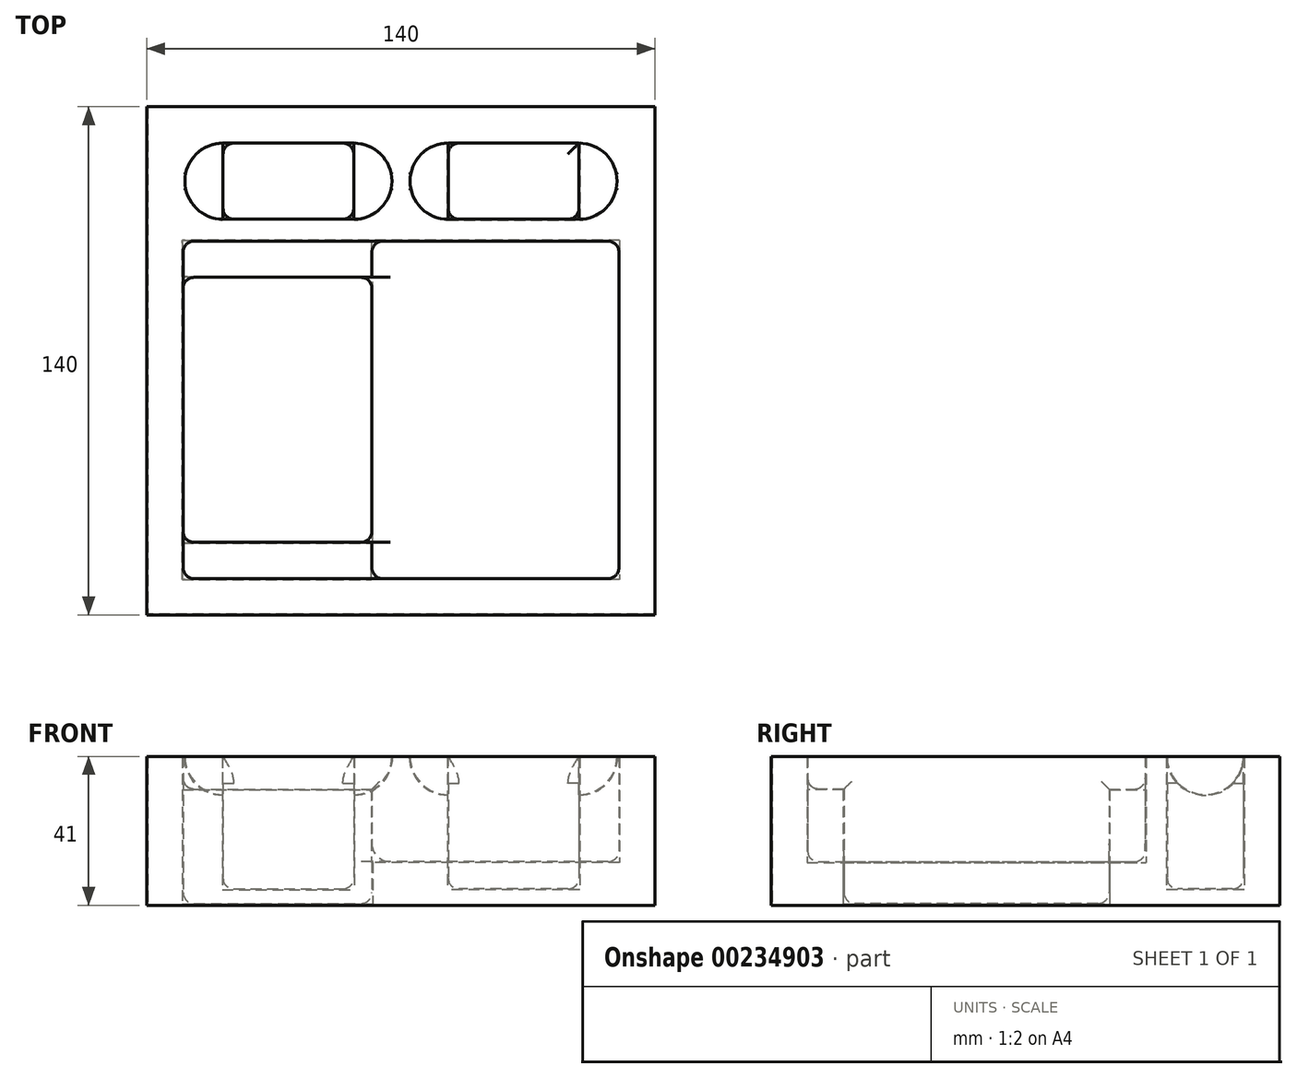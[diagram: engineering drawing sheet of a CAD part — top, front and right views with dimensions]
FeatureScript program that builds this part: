
annotation { "Feature Type Name" : "Feature", "Feature Type Description" : "" }
export const myFeature = defineFeature(function(context is Context, id is Id, definition is map)
    precondition{}
    {
        {
            var Q0;
            Q0=qCreatedBy(makeId("Top.planeOp"),FACE);
            cPlane(context, id + "F0", {"entities" : qUnion([Q0]), "cplaneType" : CPlaneType.OFFSET, "offset" : 4.5 * mm, "width" : 150 * mm, "height" : 150 * mm});
        }
        {
            var Q0;
            Q0=qCreatedBy(makeId("Top.planeOp"),FACE);
            cPlane(context, id + "F1", {"entities" : qUnion([Q0]), "cplaneType" : CPlaneType.OFFSET, "offset" : .5 * mm, "width" : 150 * mm, "height" : 150 * mm});
        }
        {
            var Q0;
            Q0=qCreatedBy(makeId("Top.planeOp"),FACE);
            cPlane(context, id + "F2", {"entities" : qUnion([Q0]), "cplaneType" : CPlaneType.OFFSET, "offset" : 12 * mm, "width" : 150 * mm, "height" : 150 * mm});
        }
        {
            var Q0;
            Q0=qCreatedBy(makeId("Top.planeOp"),FACE);
            cPlane(context, id + "F3", {"entities" : qUnion([Q0]), "cplaneType" : CPlaneType.OFFSET, "offset" : 32 * mm, "width" : 150 * mm, "height" : 150 * mm});
        }
        {
            var Q0;
            Q0=qCreatedBy(makeId("Top.planeOp"),FACE);
            var sketch = newSketch(context, id + "F4", { "sketchPlane" : qUnion([Q0])});
            skLineSegment(sketch, "E0.bottom", {"start": v(70, 70) * mm, "end": v(-70, 70) * mm});
            skLineSegment(sketch, "E0.top", {"start": v(70, -70) * mm, "end": v(-70, -70) * mm});
            skLineSegment(sketch, "E0.left", {"start": v(70, 70) * mm, "end": v(70, -70) * mm});
            skLineSegment(sketch, "E0.right", {"start": v(-70, 70) * mm, "end": v(-70, -70) * mm});
            skPoint(sketch, "E0.middle", {"position": v(0, 0) * mm});
            skLineSegment(sketch, "E1.0", {"start": v(60, 60) * mm, "end": v(60, -60) * mm, "construction": true});
            skLineSegment(sketch, "E1.1", {"start": v(60, 60) * mm, "end": v(-60, 60) * mm, "construction": true});
            skLineSegment(sketch, "E1.2", {"start": v(-60, 60) * mm, "end": v(-60, -60) * mm, "construction": true});
            skLineSegment(sketch, "E1.3", {"start": v(60, -60) * mm, "end": v(-60, -60) * mm, "construction": true});
            skSolve(sketch);
        }
        {
            var Q0;
            Q0 = qSketchRegion(id + "F4", true);
            extrude(context, id + "F5", {"entities" : qUnion([Q0]), "depth" : 41 * mm});
        }
        {
            var Q0;
            Q0=qCreatedBy(id+"F3.planeOp",FACE);
            var sketch = newSketch(context, id + "F6", { "sketchPlane" : qUnion([Q0])});
            skLineSegment(sketch, "E2.bottom", {"start": v(-60, -60) * mm, "end": v(33, -60) * mm});
            skLineSegment(sketch, "E2.top", {"start": v(-60, 33) * mm, "end": v(33, 33) * mm});
            skLineSegment(sketch, "E2.left", {"start": v(-60, -60) * mm, "end": v(-60, 33) * mm});
            skLineSegment(sketch, "E2.right", {"start": v(33, -60) * mm, "end": v(33, 33) * mm});
            skSolve(sketch);
        }
        {
            var Q0;
            Q0 = qSketchRegion(id + "F6", true);
            extrude(context, id + "F7", {"entities" : qUnion([Q0]), "operationType" : NewBodyOperationType.REMOVE, "endBound" : BoundingType.THROUGH_ALL, "depth" : 7.5 * mm});
        }
        {
            var Q0;
            Q0=qCreatedBy(id+"F0.planeOp",FACE);
            var sketch = newSketch(context, id + "F8", { "sketchPlane" : qUnion([Q0])});
            skLineSegment(sketch, "E3.bottom", {"start": v(-49, 60) * mm, "end": v(-13, 60) * mm});
            skLineSegment(sketch, "E3.top", {"start": v(-49, 39) * mm, "end": v(-13, 39) * mm});
            skLineSegment(sketch, "E3.left", {"start": v(-49, 60) * mm, "end": v(-49, 39) * mm});
            skLineSegment(sketch, "E3.right", {"start": v(-13, 60) * mm, "end": v(-13, 39) * mm});
            skLineSegment(sketch, "E4.MirrorCS", {"start": v(49, 39) * mm, "end": v(13, 39) * mm});
            skLineSegment(sketch, "E5.MirrorCS", {"start": v(49, 60) * mm, "end": v(13, 60) * mm});
            skLineSegment(sketch, "E6.MirrorCS", {"start": v(49, 60) * mm, "end": v(49, 39) * mm});
            skLineSegment(sketch, "E7.MirrorCS", {"start": v(13, 60) * mm, "end": v(13, 39) * mm});
            skSolve(sketch);
        }
        {
            var Q0;
            Q0 = qSketchRegion(id + "F8", true);
            extrude(context, id + "F9", {"entities" : qUnion([Q0]), "operationType" : NewBodyOperationType.REMOVE, "endBound" : BoundingType.THROUGH_ALL, "depth" : 35 * mm});
        }
        {
            var Q0;
            Q0=qCreatedBy(id+"F2.planeOp",FACE);
            var sketch = newSketch(context, id + "F10", { "sketchPlane" : qUnion([Q0])});
            skLineSegment(sketch, "E8.bottom", {"start": v(60, -60) * mm, "end": v(-8, -60) * mm});
            skLineSegment(sketch, "E8.top", {"start": v(60, 33) * mm, "end": v(-8, 33) * mm});
            skLineSegment(sketch, "E8.left", {"start": v(60, -60) * mm, "end": v(60, 33) * mm});
            skLineSegment(sketch, "E8.right", {"start": v(-8, -60) * mm, "end": v(-8, 33) * mm});
            skSolve(sketch);
        }
        {
            var Q0;
            Q0 = qSketchRegion(id + "F10", true);
            extrude(context, id + "F11", {"entities" : qUnion([Q0]), "operationType" : NewBodyOperationType.REMOVE, "endBound" : BoundingType.THROUGH_ALL, "depth" : 22 * mm});
        }
        {
            var Q0;
            Q0=qCreatedBy(id+"F1.planeOp",FACE);
            var sketch = newSketch(context, id + "F12", { "sketchPlane" : qUnion([Q0])});
            skLineSegment(sketch, "E9.bottom", {"start": v(-60, -50) * mm, "end": v(-8, -50) * mm});
            skLineSegment(sketch, "E9.top", {"start": v(-60, 23) * mm, "end": v(-8, 23) * mm});
            skLineSegment(sketch, "E9.left", {"start": v(-60, -50) * mm, "end": v(-60, 23) * mm});
            skLineSegment(sketch, "E10", {"start": v(-60, -13.5) * mm, "end": v(-65.69, -13.5) * mm, "construction": true});
            skPoint(sketch, "E10.endSnap0", {"position": v(-60, -13.5) * mm});
            skLineSegment(sketch, "E11", {"start": v(-8, 23) * mm, "end": v(-8, -50) * mm});
            skSolve(sketch);
        }
        {
            var Q0;
            Q0 = qSketchRegion(id + "F12", true);
            extrude(context, id + "F13", {"entities" : qUnion([Q0]), "operationType" : NewBodyOperationType.REMOVE, "endBound" : BoundingType.THROUGH_ALL, "depth" : 25 * mm});
        }
        {
            var Q0;
            Q0=makeQuery(id+"F5.opExtrude","CAP_FACE",FACE,{"disambiguationData":[OSD([sQuery(id+"F4.wireOp",EDGE,"E0.bottom"),sQuery(id+"F4.wireOp",EDGE,"E0.top"),sQuery(id+"F4.wireOp",EDGE,"E0.left"),sQuery(id+"F4.wireOp",EDGE,"E0.right")])],"isStart":false});
            var sketch = newSketch(context, id + "F14", { "sketchPlane" : qUnion([Q0])});
            skLineSegment(sketch, "E12", {"start": v(-59.5, 49.5) * mm, "end": v(-38.5, 49.5) * mm});
            skArc(sketch, "E13", {"start": v(-59.5, 49.5) * mm, "mid": v(-49, 60) * mm, "end": v(-38.5, 49.5) * mm});
            skArc(sketch, "E14", {"start": v(-23.5, 49.5) * mm, "mid": v(-13, 60) * mm, "end": v(-2.5, 49.5) * mm});
            skArc(sketch, "E15", {"start": v(38.5, 49.5) * mm, "mid": v(49, 60) * mm, "end": v(59.5, 49.5) * mm});
            skArc(sketch, "E16", {"start": v(2.5, 49.5) * mm, "mid": v(13, 60) * mm, "end": v(23.5, 49.5) * mm});
            skLineSegment(sketch, "E17.trimOffspring", {"start": v(-23.5, 49.5) * mm, "end": v(-2.5, 49.5) * mm});
            skLineSegment(sketch, "E18.trimOffspring", {"start": v(2.5, 49.5) * mm, "end": v(23.5, 49.5) * mm});
            skLineSegment(sketch, "E19.trimOffspring", {"start": v(38.5, 49.5) * mm, "end": v(59.5, 49.5) * mm});
            skSolve(sketch);
        }
        {
            var Q0;
            Q0 = qSketchRegion(id + "F14", true);
            var Q1;
            Q1=sQuery(id+"F14.wireOp",EDGE,"E17.trimOffspring");
            revolve(context, id + "F15", {"operationType" : NewBodyOperationType.REMOVE, "entities" : qUnion([Q0]), "axis" : qUnion([Q1]), "revolveType" : RevolveType.ONE_DIRECTION, "oppositeDirection" : true, "angle" : 180 * degree});
        }
        {
            var Q0;
            Q0=makeQuery(id+"F5.opExtrude","CAP_FACE",FACE,{"disambiguationData":[OSD([sQuery(id+"F4.wireOp",EDGE,"E0.bottom"),sQuery(id+"F4.wireOp",EDGE,"E0.top"),sQuery(id+"F4.wireOp",EDGE,"E0.left"),sQuery(id+"F4.wireOp",EDGE,"E0.right")])],"isStart":true});
            shell(context, id + "F16", {"entities" : qUnion([Q0]), "thickness" : .2 * mm});
        }
        {
            var Q0;
            Q0=makeQuery(id+"F7.boolean.opBoolean","COPY",EDGE,{"derivedFrom":makeQuery(id+"F7.opExtrude","CAP_EDGE",EDGE,{"disambiguationData":[OSD([sQuery(id+"F6.wireOp",EDGE,"E2.top")])],"isStart":true})});
            var Q1;
            {var subQ0=sQuery(id+"F6.wireOp",EDGE,"E2.left");var subQ1=sQuery(id+"F6.wireOp",EDGE,"E2.top");Q1=makeQuery(id+"F13.boolean.opBoolean","SPLIT",EDGE,{"disambiguationData":[TD([makeQuery(id+"F7.boolean.opBoolean","COPY",FACE,{"derivedFrom":makeQuery(id+"F7.opExtrude","SWEPT_FACE",FACE,{"disambiguationData":[OSD([subQ1])]})})])],"derivedFrom":makeQuery(id+"F7.boolean.opBoolean","COPY",EDGE,{"derivedFrom":makeQuery(id+"F7.opExtrude","CAP_EDGE",EDGE,{"disambiguationData":[OSD([subQ0])],"isStart":true})})});}
            var Q2;
            Q2=makeQuery(id+"F13.boolean.opBoolean","COPY",EDGE,{"derivedFrom":makeQuery(id+"F13.opExtrude","SWEPT_EDGE",EDGE,{"disambiguationData":[OSD([sQuery(id+"F12.wireOp",EDGE,"E9.top"),sQuery(id+"F12.wireOp",EDGE,"E9.left")])]})});
            var Q3;
            Q3=makeQuery(id+"F11.boolean.opBoolean","COPY",EDGE,{"derivedFrom":makeQuery(id+"F11.opExtrude","SWEPT_EDGE",EDGE,{"disambiguationData":[OSD([sQuery(id+"F10.wireOp",EDGE,"E8.top"),sQuery(id+"F10.wireOp",EDGE,"E8.right")])]})});
            var Q4;
            Q4=makeQuery(id+"F13.boolean.opBoolean","COPY",EDGE,{"derivedFrom":makeQuery(id+"F13.opExtrude","CAP_EDGE",EDGE,{"disambiguationData":[OSD([sQuery(id+"F12.wireOp",EDGE,"E9.top")])],"isStart":true})});
            var Q5;
            Q5=makeQuery(id+"F13.boolean.opBoolean","COPY",EDGE,{"derivedFrom":makeQuery(id+"F13.opExtrude","CAP_EDGE",EDGE,{"disambiguationData":[OSD([sQuery(id+"F12.wireOp",EDGE,"E9.left")])],"isStart":true})});
            var Q6;
            Q6=makeQuery(id+"F11.boolean.opBoolean","COPY",EDGE,{"derivedFrom":makeQuery(id+"F11.opExtrude","CAP_EDGE",EDGE,{"disambiguationData":[OSD([sQuery(id+"F10.wireOp",EDGE,"E8.top")])],"isStart":true})});
            var Q7;
            Q7=makeQuery(id+"F7.boolean.opBoolean","COPY",EDGE,{"derivedFrom":makeQuery(id+"F7.opExtrude","SWEPT_EDGE",EDGE,{"disambiguationData":[OSD([sQuery(id+"F6.wireOp",EDGE,"E2.top"),sQuery(id+"F6.wireOp",EDGE,"E2.left")])]})});
            var Q8;
            Q8=makeQuery(id+"F11.boolean.opBoolean","COPY",EDGE,{"derivedFrom":makeQuery(id+"F11.opExtrude","SWEPT_EDGE",EDGE,{"disambiguationData":[OSD([sQuery(id+"F10.wireOp",EDGE,"E8.top"),sQuery(id+"F10.wireOp",EDGE,"E8.left")])]})});
            var Q9;
            Q9=makeQuery(id+"F11.boolean.opBoolean","COPY",EDGE,{"derivedFrom":makeQuery(id+"F11.opExtrude","CAP_EDGE",EDGE,{"disambiguationData":[OSD([sQuery(id+"F10.wireOp",EDGE,"E8.left")])],"isStart":true})});
            var Q10;
            Q10=makeQuery(id+"F11.boolean.opBoolean","COPY",EDGE,{"derivedFrom":makeQuery(id+"F11.opExtrude","CAP_EDGE",EDGE,{"disambiguationData":[OSD([sQuery(id+"F10.wireOp",EDGE,"E8.bottom")])],"isStart":true})});
            var Q11;
            Q11=makeQuery(id+"F13.boolean.opBoolean","COPY",EDGE,{"derivedFrom":makeQuery(id+"F13.opExtrude","CAP_EDGE",EDGE,{"disambiguationData":[OSD([sQuery(id+"F12.wireOp",EDGE,"E9.bottom")])],"isStart":true})});
            var Q12;
            {var subQ0=sQuery(id+"F12.wireOp",EDGE,"E9.bottom");var subQ2=sQuery(id+"F12.wireOp",EDGE,"E11");Q12=makeQuery(id+"F13.boolean.opBoolean","COPY",EDGE,{"disambiguationData":[TD([makeQuery(id+"F13.opExtrude","CAP_FACE",FACE,{"disambiguationData":[OSD([subQ0,sQuery(id+"F12.wireOp",EDGE,"E9.top"),sQuery(id+"F12.wireOp",EDGE,"E9.left"),subQ2])],"isStart":true})])],"derivedFrom":makeQuery(id+"F13.opExtrude","SWEPT_EDGE",EDGE,{"disambiguationData":[OSD([subQ0,subQ2])]})});}
            var Q13;
            Q13=makeQuery(id+"F13.boolean.opBoolean","COPY",EDGE,{"derivedFrom":makeQuery(id+"F13.opExtrude","CAP_EDGE",EDGE,{"disambiguationData":[OSD([sQuery(id+"F12.wireOp",EDGE,"E11")])],"isStart":true})});
            var Q14;
            {var subQ0=sQuery(id+"F12.wireOp",EDGE,"E9.top");var subQ1=sQuery(id+"F12.wireOp",EDGE,"E11");Q14=makeQuery(id+"F13.boolean.opBoolean","COPY",EDGE,{"disambiguationData":[TD([makeQuery(id+"F13.opExtrude","CAP_FACE",FACE,{"disambiguationData":[OSD([sQuery(id+"F12.wireOp",EDGE,"E9.bottom"),subQ0,sQuery(id+"F12.wireOp",EDGE,"E9.left"),subQ1])],"isStart":true})])],"derivedFrom":makeQuery(id+"F13.opExtrude","SWEPT_EDGE",EDGE,{"disambiguationData":[OSD([subQ0,subQ1])]})});}
            var Q15;
            Q15=makeQuery(id+"F13.boolean.opBoolean","COPY",EDGE,{"derivedFrom":makeQuery(id+"F13.opExtrude","SWEPT_EDGE",EDGE,{"disambiguationData":[OSD([sQuery(id+"F12.wireOp",EDGE,"E9.bottom"),sQuery(id+"F12.wireOp",EDGE,"E9.left")])]})});
            var Q16;
            Q16=makeQuery(id+"F7.boolean.opBoolean","COPY",EDGE,{"derivedFrom":makeQuery(id+"F7.opExtrude","SWEPT_EDGE",EDGE,{"disambiguationData":[OSD([sQuery(id+"F6.wireOp",EDGE,"E2.bottom"),sQuery(id+"F6.wireOp",EDGE,"E2.left")])]})});
            var Q17;
            {var subQ0=sQuery(id+"F6.wireOp",EDGE,"E2.left");var subQ1=sQuery(id+"F6.wireOp",EDGE,"E2.bottom");Q17=makeQuery(id+"F13.boolean.opBoolean","SPLIT",EDGE,{"disambiguationData":[TD([makeQuery(id+"F7.boolean.opBoolean","COPY",FACE,{"derivedFrom":makeQuery(id+"F7.opExtrude","SWEPT_FACE",FACE,{"disambiguationData":[OSD([subQ1])]})})])],"derivedFrom":makeQuery(id+"F7.boolean.opBoolean","COPY",EDGE,{"derivedFrom":makeQuery(id+"F7.opExtrude","CAP_EDGE",EDGE,{"disambiguationData":[OSD([subQ0])],"isStart":true})})});}
            var Q18;
            Q18=makeQuery(id+"F7.boolean.opBoolean","COPY",EDGE,{"derivedFrom":makeQuery(id+"F7.opExtrude","CAP_EDGE",EDGE,{"disambiguationData":[OSD([sQuery(id+"F6.wireOp",EDGE,"E2.bottom")])],"isStart":true})});
            var Q19;
            Q19=makeQuery(id+"F11.boolean.opBoolean","COPY",EDGE,{"derivedFrom":makeQuery(id+"F11.opExtrude","SWEPT_EDGE",EDGE,{"disambiguationData":[OSD([sQuery(id+"F10.wireOp",EDGE,"E8.bottom"),sQuery(id+"F10.wireOp",EDGE,"E8.right")])]})});
            var Q20;
            Q20=makeQuery(id+"F11.boolean.opBoolean","COPY",EDGE,{"derivedFrom":makeQuery(id+"F11.opExtrude","SWEPT_EDGE",EDGE,{"disambiguationData":[OSD([sQuery(id+"F10.wireOp",EDGE,"E8.bottom"),sQuery(id+"F10.wireOp",EDGE,"E8.left")])]})});
            fillet(context, id + "F17", {"entities" : qUnion([Q0, Q1, Q2, Q3, Q4, Q5, Q6, Q7, Q8, Q9, Q10, Q11, Q12, Q13, Q14, Q15, Q16, Q17, Q18, Q19, Q20]), "radius" : 3 * mm, "tangentPropagation" : true, "allowEdgeOverflow" : false});
        }
        {
            var Q0;
            {var subQ0=sQuery(id+"F10.wireOp",EDGE,"E8.right");var subQ1=sQuery(id+"F10.wireOp",EDGE,"E8.top");Q0=makeQuery(id+"F13.boolean.opBoolean","SPLIT",EDGE,{"disambiguationData":[TD([makeQuery(id+"F7.boolean.opBoolean","COPY",FACE,{"derivedFrom":makeQuery(id+"F7.opExtrude","SWEPT_FACE",FACE,{"disambiguationData":[OSD([sQuery(id+"F6.wireOp",EDGE,"E2.top")])]})}),makeQuery(id+"F11.opExtrude","SWEPT_FACE",FACE,{"disambiguationData":[OSD([subQ1])]}),makeQuery(id+"F11.boolean.opBoolean","COPY",FACE,{"derivedFrom":makeQuery(id+"F11.opExtrude","CAP_FACE",FACE,{"disambiguationData":[OSD([sQuery(id+"F10.wireOp",EDGE,"E8.bottom"),subQ1,sQuery(id+"F10.wireOp",EDGE,"E8.left"),subQ0])],"isStart":true})}),makeQuery(id+"F11.boolean.opBoolean","COPY",FACE,{"derivedFrom":makeQuery(id+"F11.opExtrude","SWEPT_FACE",FACE,{"disambiguationData":[OSD([subQ0])]})}),makeQuery(id+"F13.opExtrude","SWEPT_FACE",FACE,{"disambiguationData":[OSD([sQuery(id+"F12.wireOp",EDGE,"E9.top")])]}),makeQuery(id+"F13.opExtrude","SWEPT_FACE",FACE,{"disambiguationData":[OSD([sQuery(id+"F12.wireOp",EDGE,"E11")])]})])],"derivedFrom":makeQuery(id+"F11.boolean.opBoolean","COPY",EDGE,{"derivedFrom":makeQuery(id+"F11.opExtrude","CAP_EDGE",EDGE,{"disambiguationData":[OSD([subQ0])],"isStart":true})})});}
            var Q1;
            {var subQ0=sQuery(id+"F10.wireOp",EDGE,"E8.right");var subQ1=sQuery(id+"F10.wireOp",EDGE,"E8.bottom");Q1=makeQuery(id+"F13.boolean.opBoolean","SPLIT",EDGE,{"disambiguationData":[TD([makeQuery(id+"F7.boolean.opBoolean","COPY",FACE,{"derivedFrom":makeQuery(id+"F7.opExtrude","SWEPT_FACE",FACE,{"disambiguationData":[OSD([sQuery(id+"F6.wireOp",EDGE,"E2.bottom")])]})}),makeQuery(id+"F11.opExtrude","SWEPT_FACE",FACE,{"disambiguationData":[OSD([subQ1])]}),makeQuery(id+"F11.boolean.opBoolean","COPY",FACE,{"derivedFrom":makeQuery(id+"F11.opExtrude","CAP_FACE",FACE,{"disambiguationData":[OSD([subQ1,sQuery(id+"F10.wireOp",EDGE,"E8.top"),sQuery(id+"F10.wireOp",EDGE,"E8.left"),subQ0])],"isStart":true})}),makeQuery(id+"F11.boolean.opBoolean","COPY",FACE,{"derivedFrom":makeQuery(id+"F11.opExtrude","SWEPT_FACE",FACE,{"disambiguationData":[OSD([subQ0])]})}),makeQuery(id+"F13.opExtrude","SWEPT_FACE",FACE,{"disambiguationData":[OSD([sQuery(id+"F12.wireOp",EDGE,"E9.bottom")])]}),makeQuery(id+"F13.opExtrude","SWEPT_FACE",FACE,{"disambiguationData":[OSD([sQuery(id+"F12.wireOp",EDGE,"E11")])]})])],"derivedFrom":makeQuery(id+"F11.boolean.opBoolean","COPY",EDGE,{"derivedFrom":makeQuery(id+"F11.opExtrude","CAP_EDGE",EDGE,{"disambiguationData":[OSD([subQ0])],"isStart":true})})});}
            fillet(context, id + "F18", {"entities" : qUnion([Q0, Q1]), "radius" : 5 * mm, "tangentPropagation" : true, "allowEdgeOverflow" : false});
        }
        {
            var Q0;
            Q0=makeQuery(id+"F9.boolean.opBoolean","COPY",FACE,{"derivedFrom":makeQuery(id+"F9.opExtrude","CAP_FACE",FACE,{"disambiguationData":[OSD([sQuery(id+"F8.wireOp",EDGE,"E3.bottom"),sQuery(id+"F8.wireOp",EDGE,"E3.top"),sQuery(id+"F8.wireOp",EDGE,"E3.left"),sQuery(id+"F8.wireOp",EDGE,"E3.right")])],"isStart":true})});
            var Q1;
            Q1=makeQuery(id+"F9.boolean.opBoolean","COPY",FACE,{"derivedFrom":makeQuery(id+"F9.opExtrude","CAP_FACE",FACE,{"disambiguationData":[OSD([sQuery(id+"F8.wireOp",EDGE,"E4.MirrorCS"),sQuery(id+"F8.wireOp",EDGE,"E5.MirrorCS"),sQuery(id+"F8.wireOp",EDGE,"E6.MirrorCS"),sQuery(id+"F8.wireOp",EDGE,"E7.MirrorCS")])],"isStart":true})});
            var Q2;
            Q2=makeQuery(id+"F9.boolean.opBoolean","COPY",EDGE,{"derivedFrom":makeQuery(id+"F9.opExtrude","SWEPT_EDGE",EDGE,{"disambiguationData":[OSD([sQuery(id+"F8.wireOp",EDGE,"E3.top"),sQuery(id+"F8.wireOp",EDGE,"E3.right")])]})});
            var Q3;
            Q3=makeQuery(id+"F9.boolean.opBoolean","COPY",EDGE,{"derivedFrom":makeQuery(id+"F9.opExtrude","SWEPT_EDGE",EDGE,{"disambiguationData":[OSD([sQuery(id+"F8.wireOp",EDGE,"E4.MirrorCS"),sQuery(id+"F8.wireOp",EDGE,"E6.MirrorCS")])]})});
            var Q4;
            Q4=makeQuery(id+"F9.boolean.opBoolean","COPY",EDGE,{"derivedFrom":makeQuery(id+"F9.opExtrude","SWEPT_EDGE",EDGE,{"disambiguationData":[OSD([sQuery(id+"F8.wireOp",EDGE,"E3.bottom"),sQuery(id+"F8.wireOp",EDGE,"E3.right")])]})});
            var Q5;
            Q5=makeQuery(id+"F9.boolean.opBoolean","COPY",EDGE,{"derivedFrom":makeQuery(id+"F9.opExtrude","SWEPT_EDGE",EDGE,{"disambiguationData":[OSD([sQuery(id+"F8.wireOp",EDGE,"E5.MirrorCS"),sQuery(id+"F8.wireOp",EDGE,"E7.MirrorCS")])]})});
            var Q6;
            Q6=makeQuery(id+"F9.boolean.opBoolean","COPY",EDGE,{"derivedFrom":makeQuery(id+"F9.opExtrude","SWEPT_EDGE",EDGE,{"disambiguationData":[OSD([sQuery(id+"F8.wireOp",EDGE,"E3.bottom"),sQuery(id+"F8.wireOp",EDGE,"E3.left")])]})});
            var Q7;
            Q7=makeQuery(id+"F9.boolean.opBoolean","COPY",EDGE,{"derivedFrom":makeQuery(id+"F9.opExtrude","SWEPT_EDGE",EDGE,{"disambiguationData":[OSD([sQuery(id+"F8.wireOp",EDGE,"E3.top"),sQuery(id+"F8.wireOp",EDGE,"E3.left")])]})});
            var Q8;
            Q8=makeQuery(id+"F9.boolean.opBoolean","COPY",EDGE,{"derivedFrom":makeQuery(id+"F9.opExtrude","SWEPT_EDGE",EDGE,{"disambiguationData":[OSD([sQuery(id+"F8.wireOp",EDGE,"E4.MirrorCS"),sQuery(id+"F8.wireOp",EDGE,"E7.MirrorCS")])]})});
            fillet(context, id + "F19", {"entities" : qUnion([Q0, Q1, Q2, Q3, Q4, Q5, Q6, Q7, Q8]), "radius" : 3 * mm, "tangentPropagation" : true, "allowEdgeOverflow" : false});
        }
    });
